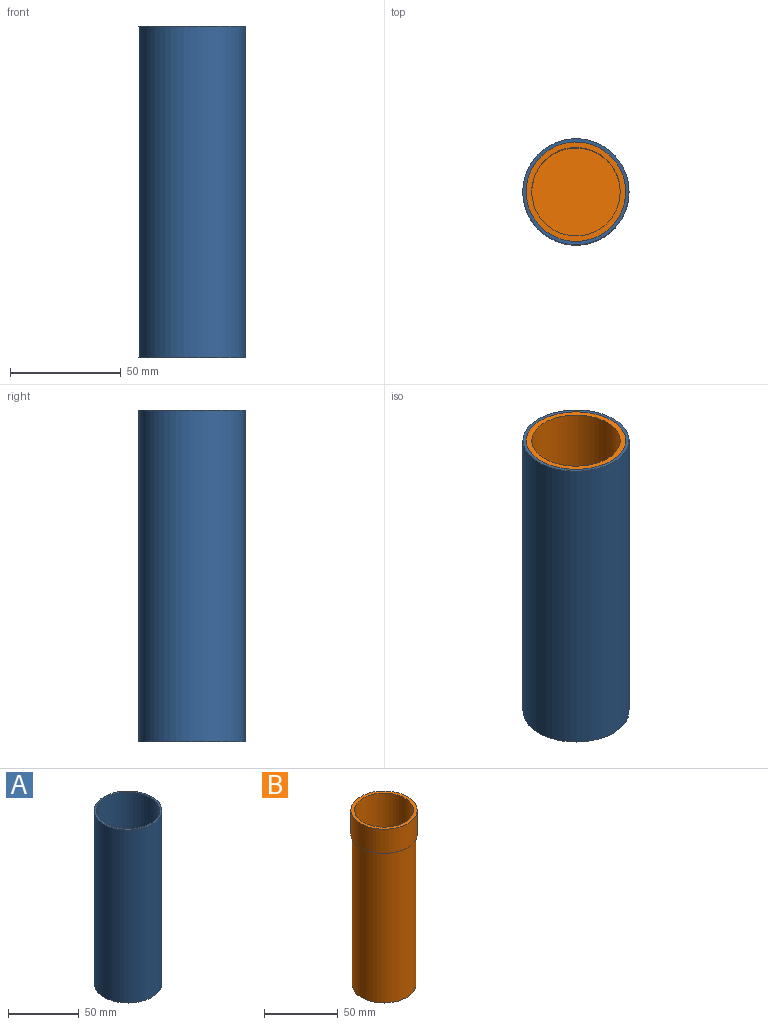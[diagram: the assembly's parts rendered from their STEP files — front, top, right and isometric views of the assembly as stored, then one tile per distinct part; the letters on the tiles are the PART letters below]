
ASSEMBLY  parts=2 mates=1
PART A: 5 faces, bbox 48x48x150 mm
  f0: cylinder r=24mm len=150mm, axis (0,0,-1), area 22619.5mm2, adj f1,f2
  f1: plane 48x48mm, normal (0,0,1), area 219.1mm2, adj f0,f3
  f2: plane 48x48mm, normal (0,0,-1), area 1809.6mm2, adj f0
  f3: cylinder r=22.5mm len=147mm, axis (0,0,1), area 20781.6mm2, adj f1,f4
  f4: plane 45x45mm, normal (0,0,1), area 1590.4mm2, adj f3
PART B: 7 faces, bbox 45x45x145 mm
  f0: cylinder r=21.5mm len=125mm, axis (0,0,-1), area 16886.1mm2, adj f1,f4
  f1: plane 43x43mm, normal (0,0,-1), area 1452.2mm2, adj f0
  f2: cylinder r=22.5mm len=45mm, axis (0,0,-1), area 2827.4mm2, adj f3,f4
  f3: plane 45x45mm, normal (0,0,1), area 333.8mm2, adj f2,f5
  f4: plane 45x45mm, normal (0,0,-1), area 138.2mm2, adj f0,f2
  f5: cylinder r=20mm len=142mm, axis (0,0,1), area 17844.2mm2, adj f3,f6
  f6: plane 40x40mm, normal (0,0,1), area 1256.6mm2, adj f5
PLACE A t=(-63.64,-3.26,-27.27)mm
PLACE B t=(-63.64,-3.26,-22.27)mm
MATE fastened A.f0 <-> B.f0  axis (0,0,1) through (-63.64,-3.26,122.73)mm
